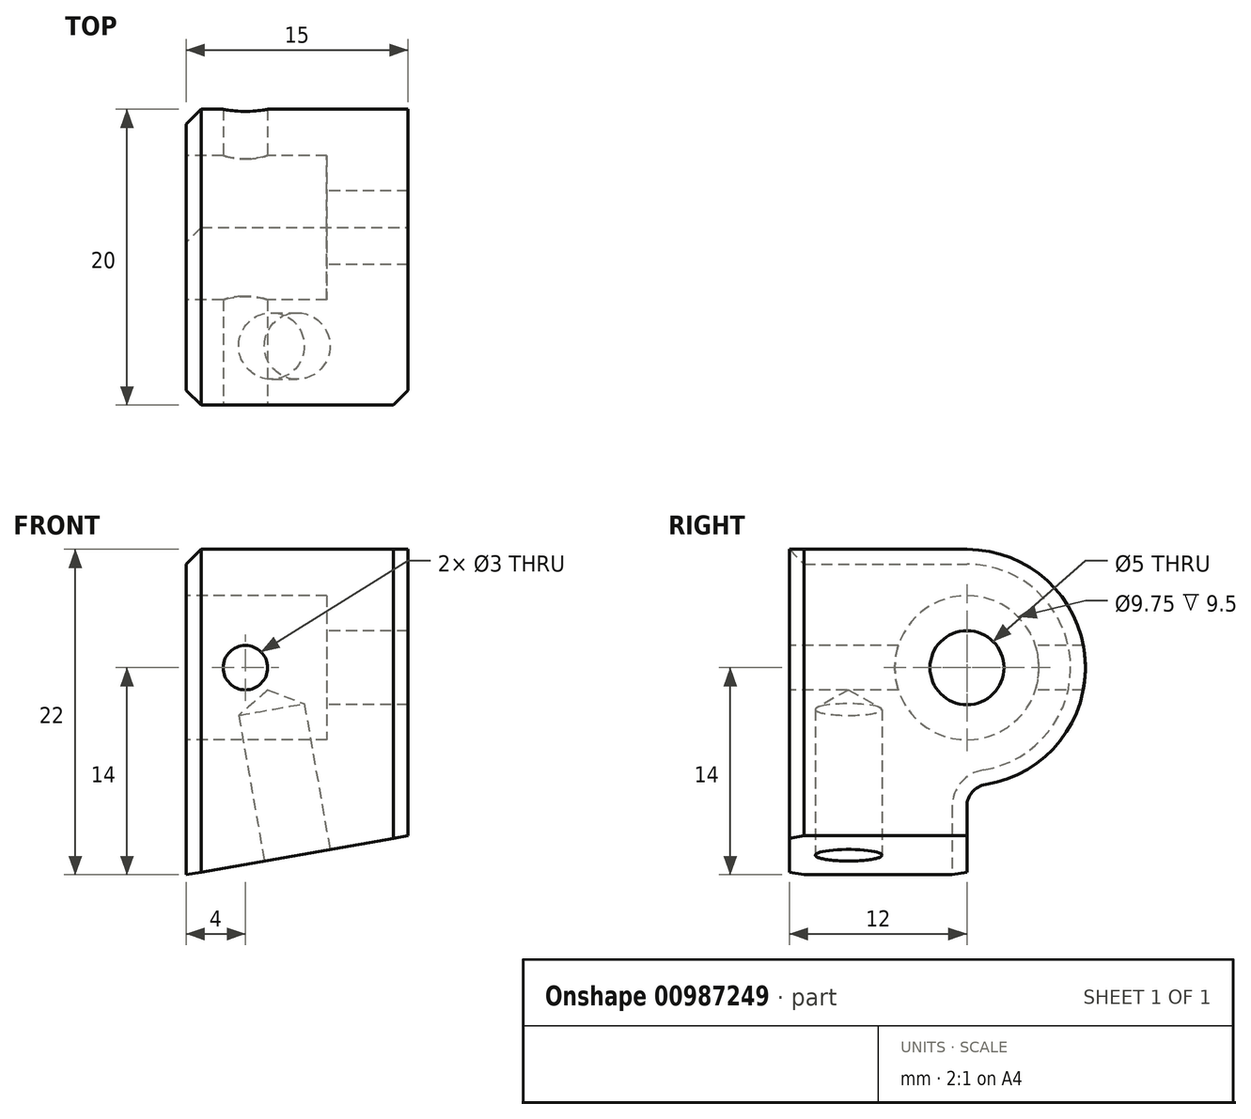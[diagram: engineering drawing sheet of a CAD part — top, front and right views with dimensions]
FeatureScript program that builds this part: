
annotation { "Feature Type Name" : "Feature", "Feature Type Description" : "" }
export const myFeature = defineFeature(function(context is Context, id is Id, definition is map)
    precondition{}
    {
        {
            var Q0;
            Q0=qCreatedBy(makeId("Front.planeOp"),FACE);
            var sketch = newSketch(context, id + "F0", { "sketchPlane" : qUnion([Q0])});
            skLineSegment(sketch, "E0", {"start": v(-7.5, 0) * mm, "end": v(-7.5, -22) * mm});
            skLineSegment(sketch, "E1", {"start": v(-7.5, -22) * mm, "end": v(7.5, -19.36) * mm});
            skLineSegment(sketch, "E2", {"start": v(7.5, -19.36) * mm, "end": v(7.5, 0) * mm});
            skLineSegment(sketch, "E3", {"start": v(7.5, 0) * mm, "end": v(-7.5, 0) * mm});
            skSolve(sketch);
        }
        {
            var Q0;
            Q0=makeQuery(id+"F0.imprint","IMPRINT",FACE,{"disambiguationData":[TD([[makeQuery(id+"F0.imprint","IMPRINT",EDGE,{"derivedFrom":sQuery(id+"F0.wireOp",EDGE,"E0")}),1.0]])]});
            extrude(context, id + "F1", {"entities" : qUnion([Q0]), "oppositeDirection" : true, "depth" : 20 * mm, "offsetDistance" : 25 * mm});
        }
        {
            var Q0;
            Q0=makeQuery(id+"F1.opExtrude","SWEPT_FACE",FACE,{"disambiguationData":[OSD([sQuery(id+"F0.wireOp",EDGE,"E0")])]});
            var sketch = newSketch(context, id + "F2", { "sketchPlane" : qUnion([Q0])});
            skPoint(sketch, "E4", {"position": v(-12, -8) * mm});
            skSolve(sketch);
        }
        {
            var Q0;
            Q0=sQuery(id+"F2.wireOp",VERTEX,"E4");
            var Q1;
            Q1=makeQuery(id+"F1.opExtrude","SWEPT_BODY",BODY,{"disambiguationData":[OSD([sQuery(id+"F0.wireOp",EDGE,"E0"),sQuery(id+"F0.wireOp",EDGE,"E1"),sQuery(id+"F0.wireOp",EDGE,"E2"),sQuery(id+"F0.wireOp",EDGE,"E3")])]});
            hole(context, id + "F3", {"style" : HoleStyle.C_BORE, "endStyle" : HoleEndStyle.THROUGH, "holeDiameter" : 5 * mm, "cBoreDiameter" : 9.75 * mm, "cBoreDepth" : 9.5 * mm, "majorDiameter" : 5 * mm, "isTappedThrough" : true, "tappedDepth" : 22.6 * mm, "tapClearance" : 3, "locations" : qUnion([Q0]), "scope" : qUnion([Q1])});
        }
        {
            var Q0;
            Q0=makeQuery(id+"F1.opExtrude","SWEPT_FACE",FACE,{"disambiguationData":[OSD([sQuery(id+"F0.wireOp",EDGE,"E1")])]});
            var sketch = newSketch(context, id + "F4", { "sketchPlane" : qUnion([Q0])});
            skPoint(sketch, "E5", {"position": v(-3.6, -4) * mm});
            skSolve(sketch);
        }
        {
            var Q0;
            Q0=sQuery(id+"F4.wireOp",VERTEX,"E5");
            var Q1;
            Q1=makeQuery(id+"F1.opExtrude","SWEPT_BODY",BODY,{"disambiguationData":[OSD([sQuery(id+"F0.wireOp",EDGE,"E0"),sQuery(id+"F0.wireOp",EDGE,"E1"),sQuery(id+"F0.wireOp",EDGE,"E2"),sQuery(id+"F0.wireOp",EDGE,"E3")])]});
            hole(context, id + "F5", {"style" : HoleStyle.SIMPLE, "endStyle" : HoleEndStyle.BLIND, "standardTappedOrClearance" : lookupTablePath({ "standard" : "ISO", "engagement" : "50%", "pitch" : "0.8 mm", "size" : "M5", "type" : "Tapped" }), "standardBlindInLast" : lookupTablePath({ "standard" : "ISO", "fit" : "Normal", "engagement" : "50%", "pitch" : "0.8 mm", "size" : "M5", "type" : "Clearance & tapped" }), "holeDiameter" : 4.5 * mm, "majorDiameter" : 5 * mm, "showTappedDepth" : true, "holeDepth" : 10 * mm, "isTappedThrough" : true, "tappedDepth" : 8.4 * mm, "tapClearance" : 2, "locations" : qUnion([Q0]), "scope" : qUnion([Q1])});
        }
        {
            var Q0;
            Q0=makeQuery(id+"F1.opExtrude","CAP_FACE",FACE,{"disambiguationData":[OSD([sQuery(id+"F0.wireOp",EDGE,"E0"),sQuery(id+"F0.wireOp",EDGE,"E1"),sQuery(id+"F0.wireOp",EDGE,"E2"),sQuery(id+"F0.wireOp",EDGE,"E3")])],"isStart":true});
            var sketch = newSketch(context, id + "F6", { "sketchPlane" : qUnion([Q0])});
            skCircle(sketch, "E6", {"center": v(-3.5, -8) * mm, "radius": 1.5 * mm});
            skSolve(sketch);
        }
        {
            var Q0;
            Q0=makeQuery(id+"F6.imprint","IMPRINT",FACE,{"disambiguationData":[TD([[makeQuery(id+"F6.imprint","IMPRINT",EDGE,{"derivedFrom":sQuery(id+"F6.wireOp",EDGE,"E6")}),1.0]])]});
            extrude(context, id + "F7", {"entities" : qUnion([Q0]), "operationType" : NewBodyOperationType.REMOVE, "endBound" : BoundingType.THROUGH_ALL, "oppositeDirection" : true, "depth" : 25 * mm, "offsetDistance" : 25 * mm});
        }
        {
            var Q0;
            Q0=makeQuery(id+"F1.opExtrude","SWEPT_FACE",FACE,{"disambiguationData":[OSD([sQuery(id+"F0.wireOp",EDGE,"E0")])]});
            var sketch = newSketch(context, id + "F8", { "sketchPlane" : qUnion([Q0])});
            skLineSegment(sketch, "E7.top", {"start": v(12.5, -25.36) * mm, "end": v(20, -25.36) * mm});
            skLineSegment(sketch, "E8", {"start": v(-12, 0) * mm, "end": v(-20, 0) * mm});
            skLineSegment(sketch, "E9", {"start": v(-20, 0) * mm, "end": v(-20, -22) * mm});
            skLineSegment(sketch, "E10", {"start": v(-20, -22) * mm, "end": v(-12, -22) * mm});
            skArc(sketch, "E11", {"start": v(-12, 0) * mm, "mid": v(-19.97, -7.37) * mm, "end": v(-13.26, -15.9) * mm});
            skLineSegment(sketch, "E12", {"start": v(-12, -17.38) * mm, "end": v(-12, -22) * mm});
            skArc(sketch, "E13", {"start": v(-12, -17.38) * mm, "mid": v(-12.36, -16.4) * mm, "end": v(-13.26, -15.9) * mm});
            skPoint(sketch, "E14.orphan", {"position": v(-12, -16) * mm});
            skSolve(sketch);
        }
        {
            var Q0;
            {var subQ0=sQuery(id+"F8.wireOp",EDGE,"E7.bottom");Q0=makeQuery(id+"F8.imprint","IMPRINT",FACE,{"disambiguationData":[TD([[makeQuery(id+"F8.imprint","IMPRINT",EDGE,{"derivedFrom":subQ0}),-1.0]])]});}
            var Q1;
            {var subQ0=sQuery(id+"F8.wireOp",EDGE,"E7.top");Q1=makeQuery(id+"F8.imprint","IMPRINT",FACE,{"disambiguationData":[TD([[makeQuery(id+"F8.imprint","IMPRINT",EDGE,{"derivedFrom":subQ0}),1.0]])]});}
            var Q2;
            {var subQ0=sQuery(id+"F8.wireOp",EDGE,"E8");Q2=makeQuery(id+"F8.imprint","IMPRINT",FACE,{"disambiguationData":[TD([[makeQuery(id+"F8.imprint","IMPRINT",EDGE,{"derivedFrom":subQ0}),-1.0]])]});}
            var Q3;
            {var subQ0=sQuery(id+"F8.wireOp",EDGE,"E10");Q3=makeQuery(id+"F8.imprint","IMPRINT",FACE,{"disambiguationData":[TD([[makeQuery(id+"F8.imprint","IMPRINT",EDGE,{"derivedFrom":subQ0}),1.0]])]});}
            extrude(context, id + "F9", {"entities" : qUnion([Q0, Q1, Q2, Q3]), "operationType" : NewBodyOperationType.REMOVE, "endBound" : BoundingType.THROUGH_ALL, "oppositeDirection" : true, "depth" : 25 * mm, "offsetDistance" : 25 * mm});
        }
        {
            var Q0;
            Q0=makeQuery(id+"F3.hole-0.boolean.opBoolean","COPY",EDGE,{"derivedFrom":makeQuery(id+"F3.hole-0.opRevolve","SWEPT_EDGE",EDGE,{"disambiguationData":[OSD([sQuery(id+"F3.hole-0.sketch.wireOp",EDGE,"cbore_start_line_2"),sQuery(id+"F3.hole-0.sketch.wireOp",EDGE,"cbore_start_line_3")])]})});
            var Q1;
            Q1=makeQuery(id+"F1.opExtrude","CAP_EDGE",EDGE,{"disambiguationData":[OSD([sQuery(id+"F0.wireOp",EDGE,"E2")])],"isStart":true});
            var Q2;
            Q2=makeQuery(id+"F1.opExtrude","CAP_EDGE",EDGE,{"disambiguationData":[OSD([sQuery(id+"F0.wireOp",EDGE,"E0")])],"isStart":true});
            var Q3;
            Q3=makeQuery(id+"F1.opExtrude","SWEPT_EDGE",EDGE,{"disambiguationData":[OSD([sQuery(id+"F0.wireOp",EDGE,"E0"),sQuery(id+"F0.wireOp",EDGE,"E3")])]});
            var Q4;
            Q4=makeQuery(id+"F9.boolean.opBoolean","COPY",EDGE,{"derivedFrom":makeQuery(id+"F9.opExtrude","CAP_EDGE",EDGE,{"disambiguationData":[OSD([sQuery(id+"F8.wireOp",EDGE,"E12")])],"isStart":true})});
            chamfer(context, id + "F10", {"entities" : qUnion([Q0, Q1, Q2, Q3, Q4]), "width" : 1 * mm, "tangentPropagation" : true});
        }
    });
